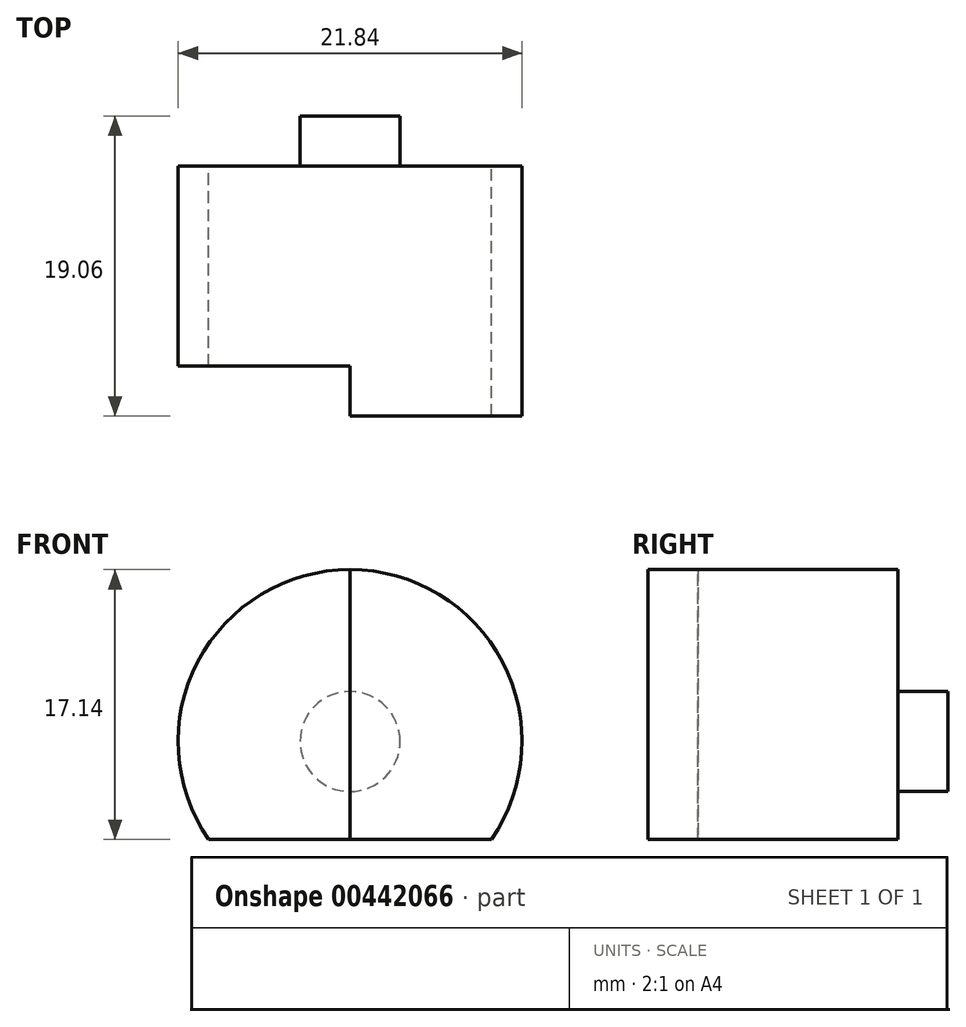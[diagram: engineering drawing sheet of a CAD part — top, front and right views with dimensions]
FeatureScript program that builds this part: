
annotation { "Feature Type Name" : "Feature", "Feature Type Description" : "" }
export const myFeature = defineFeature(function(context is Context, id is Id, definition is map)
    precondition{}
    {
        {
            var Q0;
            Q0=qCreatedBy(makeId("Front.planeOp"),FACE);
            var sketch = newSketch(context, id + "F0", { "sketchPlane" : qUnion([Q0])});
            skLineSegment(sketch, "E0", {"start": v(-12.99, 0) * mm, "end": v(13.92, 0) * mm});
            skLineSegment(sketch, "E1", {"start": v(0, 13.67) * mm, "end": v(0, -8.77) * mm});
            skArc(sketch, "E2", {"start": v(8.98, -6.22) * mm, "mid": v(0, 10.92) * mm, "end": v(-8.98, -6.22) * mm});
            skLineSegment(sketch, "E3.0", {"start": v(-8.98, -6.22) * mm, "end": v(8.98, -6.22) * mm});
            skSolve(sketch);
        }
        {
            var Q0;
            {var subQ0=sQuery(id+"F0.wireOp",EDGE,"E2");var subQ1=sQuery(id+"F0.wireOp",EDGE,"E0");var subQ2=makeQuery(id+"F0.imprint","INTERSECT",VERTEX,{"disambiguationData":[OD(1.0)],"derivedFrom":[subQ1,subQ0]});Q0=makeQuery(id+"F0.imprint","IMPRINT",FACE,{"disambiguationData":[TD([[makeQuery(id+"F0.imprint","IMPRINT",EDGE,{"disambiguationData":[TD([[subQ2,1.0]])],"derivedFrom":subQ1}),1.0]])]});}
            var Q1;
            {var subQ0=sQuery(id+"F0.wireOp",EDGE,"E2");var subQ1=sQuery(id+"F0.wireOp",EDGE,"E0");var subQ2=makeQuery(id+"F0.imprint","INTERSECT",VERTEX,{"disambiguationData":[OD(1.0)],"derivedFrom":[subQ1,subQ0]});Q1=makeQuery(id+"F0.imprint","IMPRINT",FACE,{"disambiguationData":[TD([[makeQuery(id+"F0.imprint","IMPRINT",EDGE,{"disambiguationData":[TD([[subQ2,1.0]])],"derivedFrom":subQ1}),-1.0]])]});}
            var Q2;
            {var subQ0=sQuery(id+"F0.wireOp",EDGE,"E2");var subQ1=sQuery(id+"F0.wireOp",EDGE,"E0");var subQ2=makeQuery(id+"F0.imprint","INTERSECT",VERTEX,{"disambiguationData":[OD(0.0)],"derivedFrom":[subQ1,subQ0]});Q2=makeQuery(id+"F0.imprint","IMPRINT",FACE,{"disambiguationData":[TD([[makeQuery(id+"F0.imprint","IMPRINT",EDGE,{"disambiguationData":[TD([[subQ2,-1.0]])],"derivedFrom":subQ1}),1.0]])]});}
            var Q3;
            {var subQ0=sQuery(id+"F0.wireOp",EDGE,"E2");var subQ1=sQuery(id+"F0.wireOp",EDGE,"E0");var subQ2=makeQuery(id+"F0.imprint","INTERSECT",VERTEX,{"disambiguationData":[OD(0.0)],"derivedFrom":[subQ1,subQ0]});Q3=makeQuery(id+"F0.imprint","IMPRINT",FACE,{"disambiguationData":[TD([[makeQuery(id+"F0.imprint","IMPRINT",EDGE,{"disambiguationData":[TD([[subQ2,-1.0]])],"derivedFrom":subQ1}),-1.0]])]});}
            extrude(context, id + "F1", {"entities" : qUnion([Q0, Q1, Q2, Q3]), "endBound" : BoundingType.SYMMETRIC, "depth" : 12.7 * mm});
        }
        {
            var Q0;
            Q0=makeQuery(id+"F1.opExtrude","CAP_FACE",FACE,{"disambiguationData":[OSD([sQuery(id+"F0.wireOp",EDGE,"E2"),sQuery(id+"F0.wireOp",EDGE,"E3.0")])],"isStart":false});
            var sketch = newSketch(context, id + "F2", { "sketchPlane" : qUnion([Q0])});
            skLineSegment(sketch, "E4", {"start": v(-13.19, 0) * mm, "end": v(13.64, 0) * mm});
            skLineSegment(sketch, "E5", {"start": v(0, -7.93) * mm, "end": v(0, 12.82) * mm});
            skPoint(sketch, "E5.endSnap0", {"position": v(0, 10.92) * mm});
            skCircle(sketch, "E6", {"center": v(0, 0) * mm, "radius": 3.18 * mm});
            skSolve(sketch);
        }
        {
            var Q0;
            {var subQ0=sQuery(id+"F2.wireOp",EDGE,"E5");var subQ1=sQuery(id+"F2.wireOp",EDGE,"E4");var subQ2=makeQuery(id+"F2.imprint","INTERSECT",VERTEX,{"derivedFrom":[subQ1,subQ0]});Q0=makeQuery(id+"F2.imprint","IMPRINT",FACE,{"disambiguationData":[TD([[makeQuery(id+"F2.imprint","IMPRINT",EDGE,{"disambiguationData":[TD([[subQ2,-1.0]])],"derivedFrom":subQ1}),-1.0]])]});}
            var Q1;
            {var subQ0=sQuery(id+"F2.wireOp",EDGE,"E5");var subQ1=sQuery(id+"F2.wireOp",EDGE,"E4");var subQ2=makeQuery(id+"F2.imprint","INTERSECT",VERTEX,{"derivedFrom":[subQ1,subQ0]});Q1=makeQuery(id+"F2.imprint","IMPRINT",FACE,{"disambiguationData":[TD([[makeQuery(id+"F2.imprint","IMPRINT",EDGE,{"disambiguationData":[TD([[subQ2,-1.0]])],"derivedFrom":subQ1}),1.0]])]});}
            var Q2;
            {var subQ0=sQuery(id+"F2.wireOp",EDGE,"E6");var subQ1=sQuery(id+"F2.wireOp",EDGE,"E4");var subQ2=makeQuery(id+"F2.imprint","INTERSECT",VERTEX,{"disambiguationData":[OD(0.0)],"derivedFrom":[subQ1,subQ0]});Q2=makeQuery(id+"F2.imprint","IMPRINT",FACE,{"disambiguationData":[TD([[makeQuery(id+"F2.imprint","IMPRINT",EDGE,{"disambiguationData":[TD([[subQ2,-1.0]])],"derivedFrom":subQ1}),1.0]])]});}
            var Q3;
            {var subQ0=sQuery(id+"F2.wireOp",EDGE,"E6");var subQ1=sQuery(id+"F2.wireOp",EDGE,"E4");var subQ2=makeQuery(id+"F2.imprint","INTERSECT",VERTEX,{"disambiguationData":[OD(0.0)],"derivedFrom":[subQ1,subQ0]});Q3=makeQuery(id+"F2.imprint","IMPRINT",FACE,{"disambiguationData":[TD([[makeQuery(id+"F2.imprint","IMPRINT",EDGE,{"disambiguationData":[TD([[subQ2,-1.0]])],"derivedFrom":subQ1}),-1.0]])]});}
            extrude(context, id + "F3", {"entities" : qUnion([Q0, Q1, Q2, Q3]), "operationType" : NewBodyOperationType.ADD, "depth" : 3.17 * mm});
        }
        {
            var Q0;
            Q0=makeQuery(id+"F1.opExtrude","CAP_FACE",FACE,{"disambiguationData":[OSD([sQuery(id+"F0.wireOp",EDGE,"E2"),sQuery(id+"F0.wireOp",EDGE,"E3.0")])],"isStart":true});
            var sketch = newSketch(context, id + "F4", { "sketchPlane" : qUnion([Q0])});
            skCircle(sketch, "E7", {"center": v(0, 0) * mm, "radius": 3.18 * mm});
            skSolve(sketch);
        }
        {
            var Q0;
            Q0=makeQuery(id+"F4.imprint","IMPRINT",FACE,{"disambiguationData":[TD([[makeQuery(id+"F4.imprint","IMPRINT",EDGE,{"derivedFrom":sQuery(id+"F4.wireOp",EDGE,"E7")}),1.0]])]});
            extrude(context, id + "F5", {"entities" : qUnion([Q0]), "operationType" : NewBodyOperationType.ADD, "depth" : 3.17 * mm});
        }
    });
